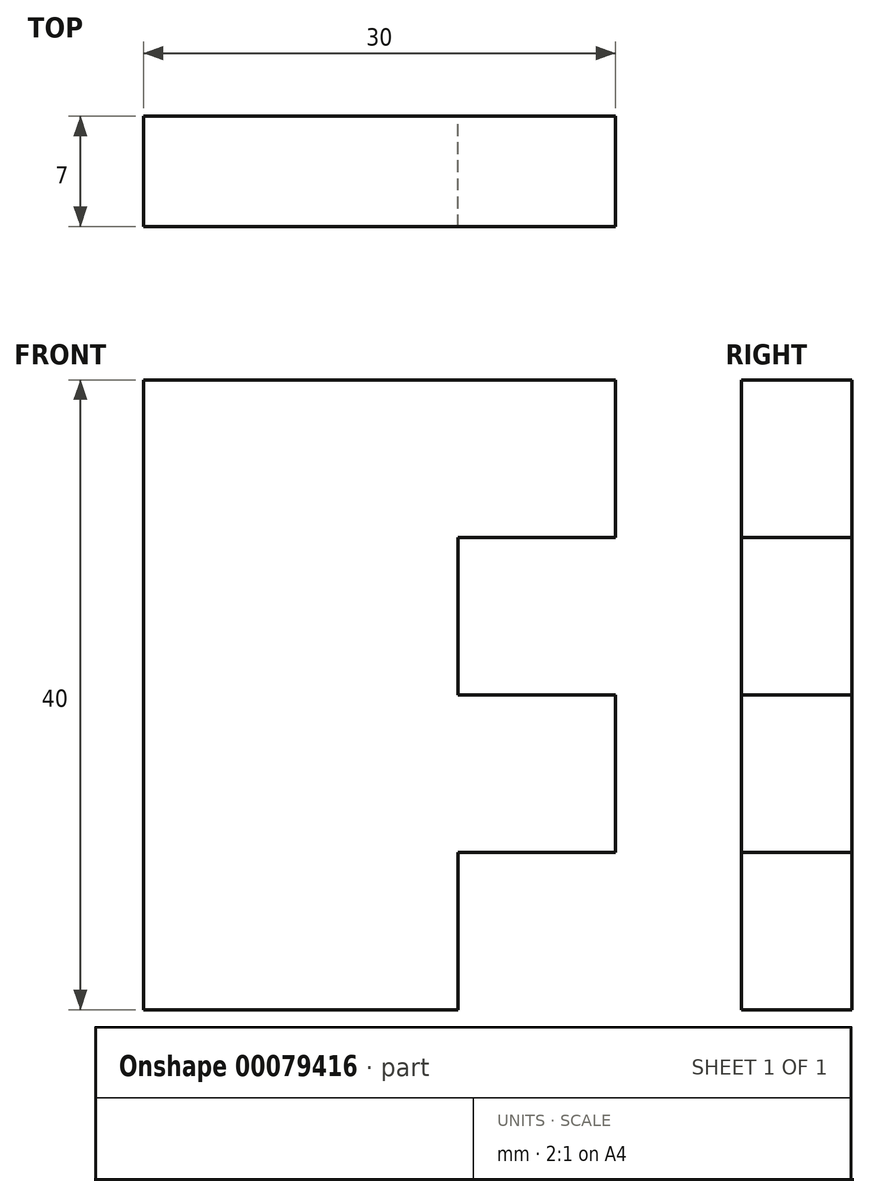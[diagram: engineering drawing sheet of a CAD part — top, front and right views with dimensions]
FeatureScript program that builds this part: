
annotation { "Feature Type Name" : "Feature", "Feature Type Description" : "" }
export const myFeature = defineFeature(function(context is Context, id is Id, definition is map)
    precondition{}
    {
        {
            var Q0;
            Q0=qCreatedBy(makeId("Top.planeOp"),FACE);
            var sketch = newSketch(context, id + "F0", { "sketchPlane" : qUnion([Q0])});
            skLineSegment(sketch, "E0.bottom", {"start": v(-30, -9.78) * mm, "end": v(-10, -9.78) * mm});
            skLineSegment(sketch, "E0.top", {"start": v(-30, -16.78) * mm, "end": v(-10, -16.78) * mm});
            skLineSegment(sketch, "E0.left", {"start": v(-30, -9.78) * mm, "end": v(-30, -16.78) * mm});
            skLineSegment(sketch, "E0.right", {"start": v(-10, -9.78) * mm, "end": v(-10, -16.78) * mm});
            skSolve(sketch);
        }
        {
            var Q0;
            Q0 = qSketchRegion(id + "F0", true);
            extrude(context, id + "F1", {"entities" : qUnion([Q0]), "depth" : 40 * mm});
        }
        {
            var Q0;
            Q0=makeQuery(id+"F1.opExtrude","SWEPT_FACE",FACE,{"disambiguationData":[OSD([sQuery(id+"F0.wireOp",EDGE,"E0.right")])]});
            var sketch = newSketch(context, id + "F2", { "sketchPlane" : qUnion([Q0])});
            skLineSegment(sketch, "E1.bottom", {"start": v(-16.78, 40) * mm, "end": v(-9.78, 40) * mm});
            skLineSegment(sketch, "E1.top", {"start": v(-16.78, 30) * mm, "end": v(-9.78, 30) * mm});
            skLineSegment(sketch, "E1.left", {"start": v(-16.78, 40) * mm, "end": v(-16.78, 30) * mm});
            skLineSegment(sketch, "E1.right", {"start": v(-9.78, 40) * mm, "end": v(-9.78, 30) * mm});
            skLineSegment(sketch, "E2.top", {"start": v(-16.78, 20) * mm, "end": v(-9.78, 20) * mm});
            skLineSegment(sketch, "E3.top", {"start": v(-16.78, 10) * mm, "end": v(-9.78, 10) * mm});
            skLineSegment(sketch, "E3.left", {"start": v(-16.78, 20) * mm, "end": v(-16.78, 10) * mm});
            skLineSegment(sketch, "E3.right", {"start": v(-9.78, 20) * mm, "end": v(-9.78, 10) * mm});
            skSolve(sketch);
        }
        {
            var Q0;
            Q0 = qSketchRegion(id + "F2", true);
            extrude(context, id + "F3", {"entities" : qUnion([Q0]), "operationType" : NewBodyOperationType.ADD, "depth" : 10 * mm});
        }
    });
